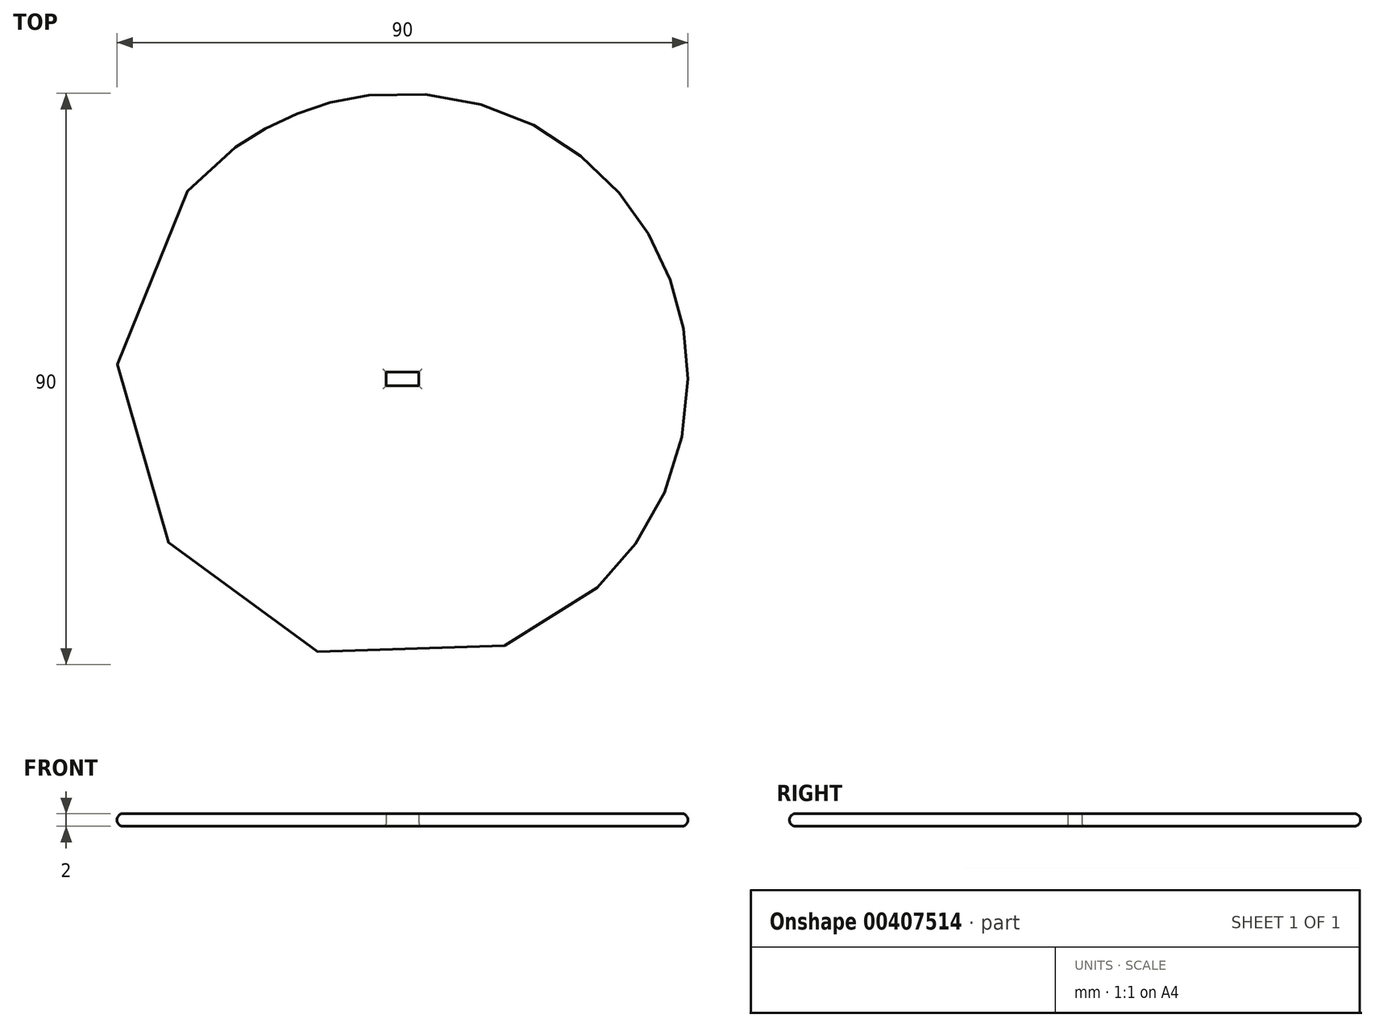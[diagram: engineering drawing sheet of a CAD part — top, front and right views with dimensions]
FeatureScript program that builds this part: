
annotation { "Feature Type Name" : "Feature", "Feature Type Description" : "" }
export const myFeature = defineFeature(function(context is Context, id is Id, definition is map)
    precondition{}
    {
        {
            var Q0;
            Q0=qCreatedBy(makeId("Top.planeOp"),FACE);
            var sketch = newSketch(context, id + "F0", { "sketchPlane" : qUnion([Q0])});
            skCircle(sketch, "E0", {"center": v(0, 0) * mm, "radius": 45 * mm});
            skLineSegment(sketch, "E1.bottom", {"start": v(2.6, -1.1) * mm, "end": v(-2.6, -1.1) * mm});
            skLineSegment(sketch, "E1.top", {"start": v(2.6, 1.1) * mm, "end": v(-2.6, 1.1) * mm});
            skLineSegment(sketch, "E1.left", {"start": v(2.6, -1.1) * mm, "end": v(2.6, 1.1) * mm});
            skLineSegment(sketch, "E1.right", {"start": v(-2.6, -1.1) * mm, "end": v(-2.6, 1.1) * mm});
            skSolve(sketch);
        }
        {
            var Q0;
            Q0=makeQuery(id+"F0.imprint","IMPRINT",FACE,{"disambiguationData":[TD([[makeQuery(id+"F0.imprint","IMPRINT",EDGE,{"derivedFrom":sQuery(id+"F0.wireOp",EDGE,"E0")}),1.0]])]});
            extrude(context, id + "F1", {"entities" : qUnion([Q0]), "depth" : 2 * mm});
        }
        {
            var Q0;
            Q0=makeQuery(id+"F1.opExtrude","CAP_EDGE",EDGE,{"disambiguationData":[OSD([sQuery(id+"F0.wireOp",EDGE,"E0")])],"isStart":false});
            fillet(context, id + "F2", {"entities" : qUnion([Q0]), "radius" : 1 * mm, "tangentPropagation" : true, "allowEdgeOverflow" : false});
        }
        {
            var Q0;
            Q0=makeQuery(id+"F1.opExtrude","CAP_EDGE",EDGE,{"disambiguationData":[OSD([sQuery(id+"F0.wireOp",EDGE,"E0")])],"isStart":true});
            fillet(context, id + "F3", {"entities" : qUnion([Q0]), "radius" : 1 * mm, "tangentPropagation" : true, "allowEdgeOverflow" : false});
        }
        {
            var Q0;
            Q0=makeQuery(id+"F1.opExtrude","CAP_EDGE",EDGE,{"disambiguationData":[OSD([sQuery(id+"F0.wireOp",EDGE,"E1.right")])],"isStart":true});
            var Q1;
            Q1=makeQuery(id+"F1.opExtrude","CAP_EDGE",EDGE,{"disambiguationData":[OSD([sQuery(id+"F0.wireOp",EDGE,"E1.bottom")])],"isStart":true});
            var Q2;
            Q2=makeQuery(id+"F1.opExtrude","CAP_EDGE",EDGE,{"disambiguationData":[OSD([sQuery(id+"F0.wireOp",EDGE,"E1.left")])],"isStart":true});
            var Q3;
            Q3=makeQuery(id+"F1.opExtrude","CAP_EDGE",EDGE,{"disambiguationData":[OSD([sQuery(id+"F0.wireOp",EDGE,"E1.top")])],"isStart":true});
            fillet(context, id + "F4", {"entities" : qUnion([Q0, Q1, Q2, Q3]), "radius" : 0.5 * mm, "tangentPropagation" : true, "allowEdgeOverflow" : false});
        }
    });
